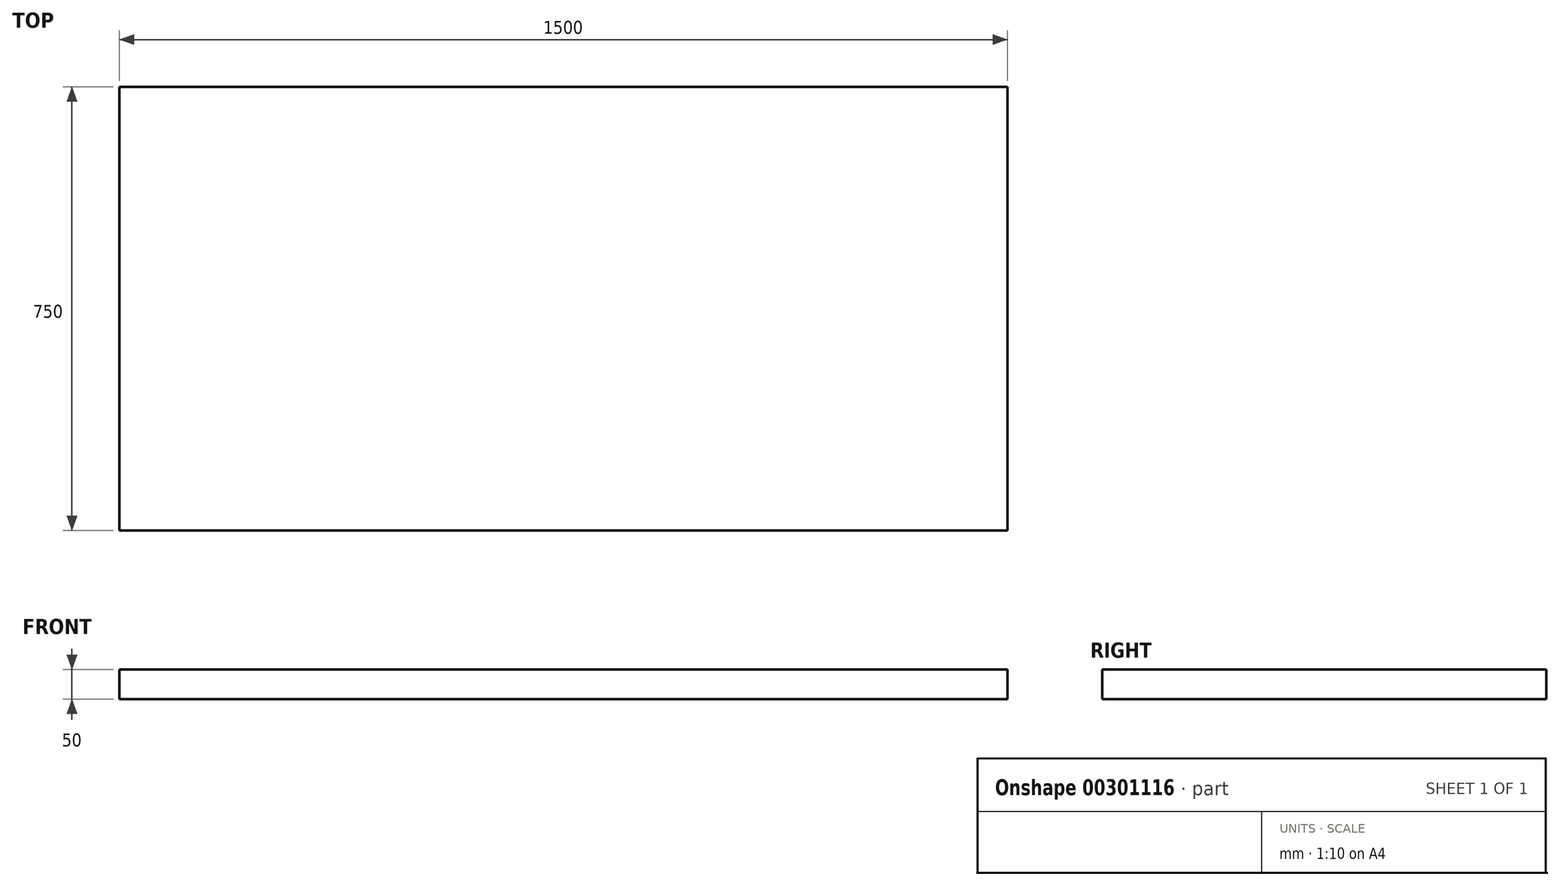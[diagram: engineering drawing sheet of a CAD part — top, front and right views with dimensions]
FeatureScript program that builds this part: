
annotation { "Feature Type Name" : "Feature", "Feature Type Description" : "" }
export const myFeature = defineFeature(function(context is Context, id is Id, definition is map)
    precondition{}
    {
        {
            var Q0;
            Q0=qCreatedBy(makeId("Top.planeOp"),FACE);
            var sketch = newSketch(context, id + "F0", { "sketchPlane" : qUnion([Q0])});
            skLineSegment(sketch, "E0.bottom", {"start": v(0, 0) * mm, "end": v(1500, 0) * mm});
            skLineSegment(sketch, "E0.top", {"start": v(0, -750) * mm, "end": v(1500, -750) * mm});
            skLineSegment(sketch, "E0.left", {"start": v(0, 0) * mm, "end": v(0, -750) * mm});
            skLineSegment(sketch, "E0.right", {"start": v(1500, 0) * mm, "end": v(1500, -750) * mm});
            skSolve(sketch);
        }
        {
            var Q0;
            Q0 = qSketchRegion(id + "F0", true);
            extrude(context, id + "F1", {"entities" : qUnion([Q0]), "depth" : 50 * mm});
        }
    });
